# Revit family: MLP 23 - MR002 - Lobe Pump
name_source: partatom
category: Specialty Equipment
units: mm (PartAtom-declared; Revit-internal decimal feet)

## family parameters
Always vertical = Yes
Cut with Voids When Loaded = No
Maintain Annotation Orientation = No
Part Type = Normal
Room Calculation Point = No
Round Connector Dimension = Use Diameter
Shared = No
Work Plane-Based = No

## types (5) — shared parameters
Description = MIT MLP 23 - Lobe Pump
Flow = 5.0 CMH
Keynote = Double Serpentine Heater Tank
Manufacturer = Ekin Endüstriyel
Pressure = 20.0 bar
URL = https://en.ekinendustriyel.com
zero-valued in all types: Default Elevation

## per-type parameters (varying)
| type | Model | Motor Power |
| MLP 23 - 1.5 kW | MLP-23 TUL - MR172 | 2 kW |
| MLP 23 - 1.1 kW | MLP-23 TUL - MR172 | 1 kW |
| MLP 23 - 2.2 kW | MLP-23 TUL - MR172 | 2 kW |
| MLP 23 - 3kW | MLP-23 TUL - MR172 | 3 kW |
| MLP 23 - 4kW | MLP-23 TUL - MR002 | 4 kW |

## geometry (parser evidence)
native form markers: Sweep x1
no freeform markers — native parametric forms only
